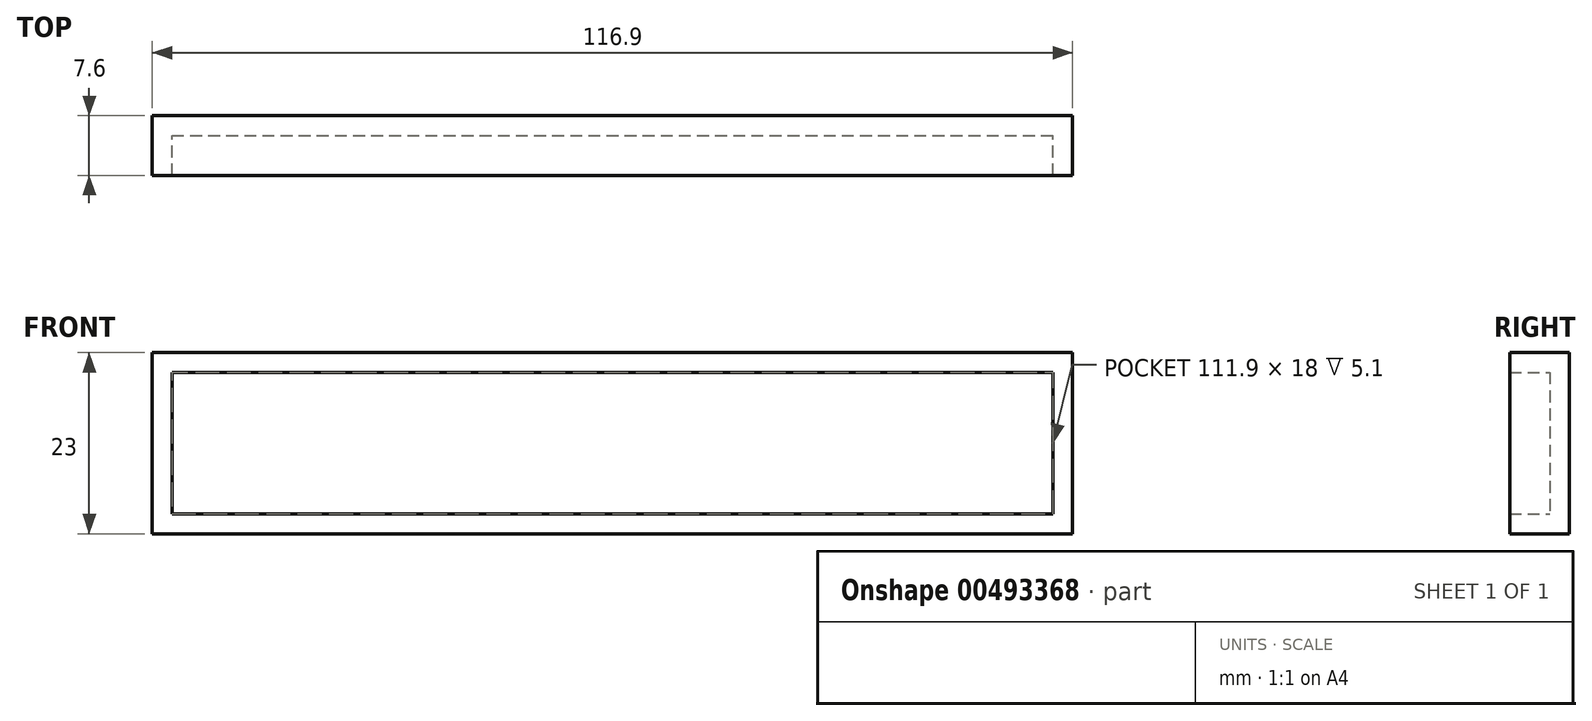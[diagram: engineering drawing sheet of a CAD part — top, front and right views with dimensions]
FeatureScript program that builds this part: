
annotation { "Feature Type Name" : "Feature", "Feature Type Description" : "" }
export const myFeature = defineFeature(function(context is Context, id is Id, definition is map)
    precondition{}
    {
        {
            var Q0;
            Q0=qCreatedBy(makeId("Front.planeOp"),FACE);
            var sketch = newSketch(context, id + "F0", { "sketchPlane" : qUnion([Q0])});
            skLineSegment(sketch, "E0.bottom", {"start": v(-41.82, 23) * mm, "end": v(75.08, 23) * mm});
            skLineSegment(sketch, "E0.top", {"start": v(-41.82, 0) * mm, "end": v(75.08, 0) * mm});
            skLineSegment(sketch, "E0.left", {"start": v(-41.82, 23) * mm, "end": v(-41.82, 0) * mm});
            skLineSegment(sketch, "E0.right", {"start": v(75.08, 23) * mm, "end": v(75.08, 0) * mm});
            skSolve(sketch);
        }
        {
            var Q0;
            Q0 = qSketchRegion(id + "F0", true);
            extrude(context, id + "F1", {"entities" : qUnion([Q0]), "endBound" : BoundingType.SYMMETRIC, "depth" : 7.6 * mm});
        }
        {
            var Q0;
            Q0=makeQuery(id+"F1.opExtrude","CAP_FACE",FACE,{"disambiguationData":[OSD([sQuery(id+"F0.wireOp",EDGE,"E0.bottom"),sQuery(id+"F0.wireOp",EDGE,"E0.top"),sQuery(id+"F0.wireOp",EDGE,"E0.left"),sQuery(id+"F0.wireOp",EDGE,"E0.right")])],"isStart":false});
            shell(context, id + "F2", {"entities" : qUnion([Q0]), "thickness" : 2.5 * mm});
        }
    });
